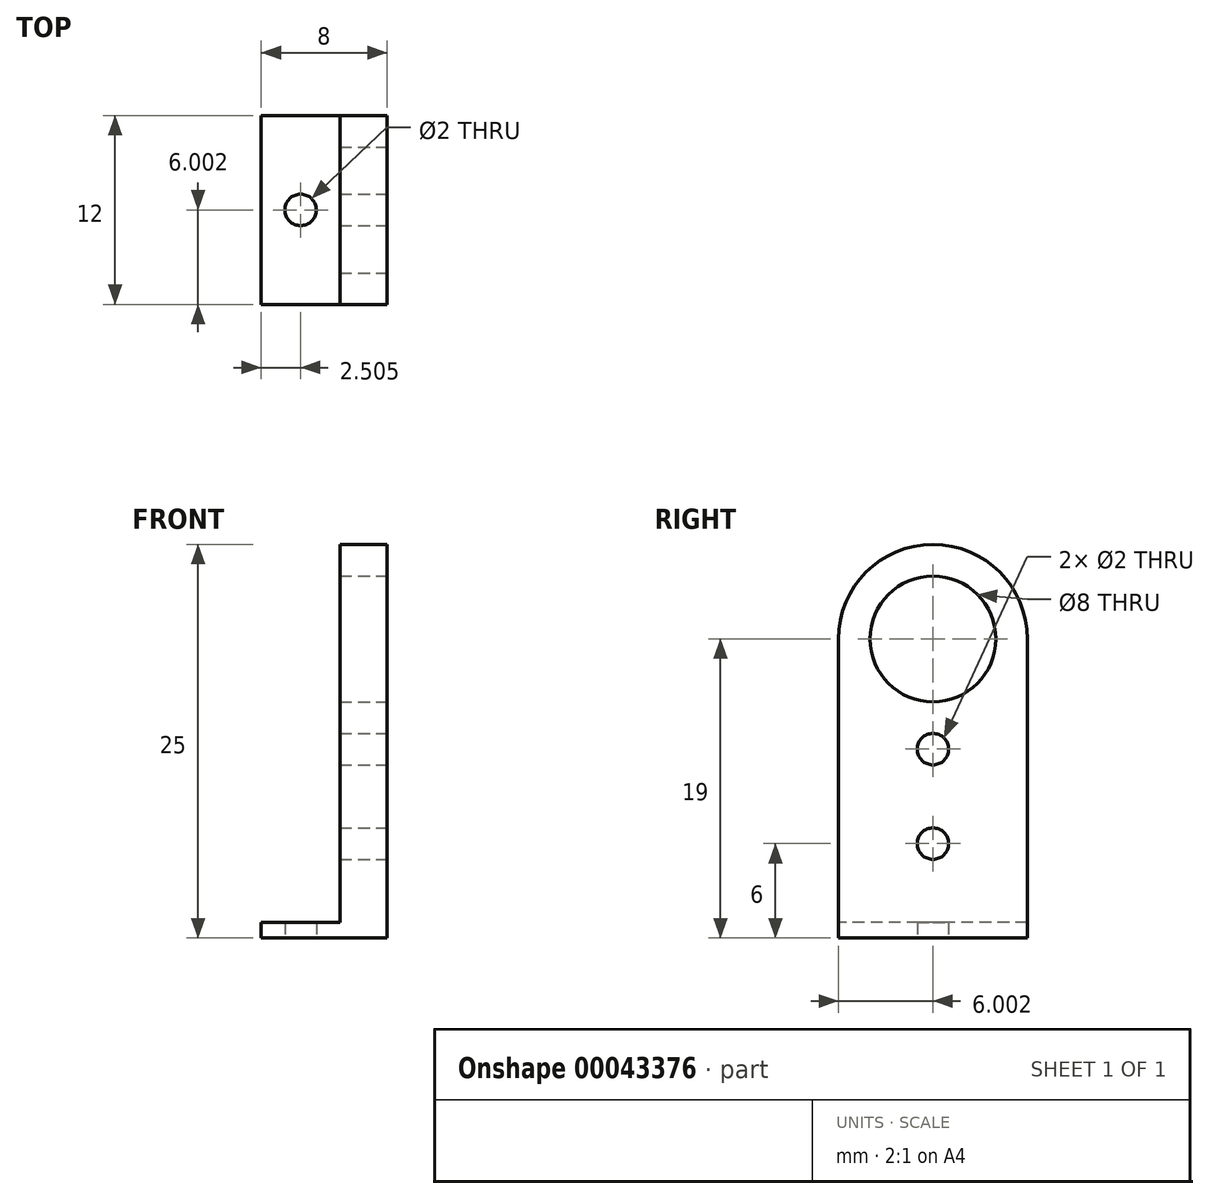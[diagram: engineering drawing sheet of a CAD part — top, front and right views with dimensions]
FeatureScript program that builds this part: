
annotation { "Feature Type Name" : "Feature", "Feature Type Description" : "" }
export const myFeature = defineFeature(function(context is Context, id is Id, definition is map)
    precondition{}
    {
        {
            var Q0;
            Q0=qCreatedBy(makeId("Top.planeOp"),FACE);
            var sketch = newSketch(context, id + "F0", { "sketchPlane" : qUnion([Q0])});
            skLineSegment(sketch, "E0.bottom", {"start": v(-17.45, 1.5) * mm, "end": v(-9.45, 1.5) * mm});
            skLineSegment(sketch, "E0.top", {"start": v(-17.45, -10.5) * mm, "end": v(-9.45, -10.5) * mm});
            skLineSegment(sketch, "E0.left", {"start": v(-17.45, 1.5) * mm, "end": v(-17.45, -10.5) * mm});
            skLineSegment(sketch, "E0.right", {"start": v(-9.45, 1.5) * mm, "end": v(-9.45, -10.5) * mm});
            skLineSegment(sketch, "E1", {"start": v(-17.45, -4.5) * mm, "end": v(-9.45, -4.5) * mm, "construction": true});
            skLineSegment(sketch, "E2", {"start": v(-13.45, 1.5) * mm, "end": v(-13.45, -10.5) * mm, "construction": true});
            skLineSegment(sketch, "E3", {"start": v(-12.45, 1.5) * mm, "end": v(-12.45, -10.5) * mm});
            skLineSegment(sketch, "E4", {"start": v(-12.45, 1.5) * mm, "end": v(-17.45, -10.5) * mm, "construction": true});
            skPoint(sketch, "E5", {"position": v(-14.95, -4.5) * mm});
            skCircle(sketch, "E6", {"center": v(-14.95, -4.5) * mm, "radius": 1 * mm});
            skSolve(sketch);
        }
        {
            var Q0;
            {var subQ2=sQuery(id+"F0.wireOp",EDGE,"E0.left");Q0=makeQuery(id+"F0.imprint","IMPRINT",FACE,{"disambiguationData":[TD([[makeQuery(id+"F0.imprint","IMPRINT",EDGE,{"derivedFrom":subQ2}),1.0]])]});}
            extrude(context, id + "F1", {"entities" : qUnion([Q0]), "depth" : 1 * mm});
        }
        {
            var Q0;
            {var subQ1=sQuery(id+"F0.wireOp",EDGE,"E0.right");Q0=makeQuery(id+"F0.imprint","IMPRINT",FACE,{"disambiguationData":[TD([[makeQuery(id+"F0.imprint","IMPRINT",EDGE,{"derivedFrom":subQ1}),-1.0]])]});}
            extrude(context, id + "F2", {"entities" : qUnion([Q0]), "operationType" : NewBodyOperationType.ADD, "depth" : 25 * mm});
        }
        {
            var Q0;
            Q0=makeQuery(id+"F2.opExtrude","SWEPT_FACE",FACE,{"disambiguationData":[OSD([sQuery(id+"F0.wireOp",EDGE,"E0.right")])]});
            var sketch = newSketch(context, id + "F3", { "sketchPlane" : qUnion([Q0])});
            skLineSegment(sketch, "E7.bottom", {"start": v(-10.5, 25) * mm, "end": v(1.5, 25) * mm, "construction": true});
            skLineSegment(sketch, "E7.top", {"start": v(-10.5, 0) * mm, "end": v(1.5, 0) * mm, "construction": true});
            skLineSegment(sketch, "E7.left", {"start": v(-10.5, 25) * mm, "end": v(-10.5, 0) * mm, "construction": true});
            skLineSegment(sketch, "E7.right", {"start": v(1.5, 25) * mm, "end": v(1.5, 0) * mm, "construction": true});
            skLineSegment(sketch, "E8", {"start": v(-4.5, 25) * mm, "end": v(-4.5, 0) * mm, "construction": true});
            skCircle(sketch, "E9", {"center": v(-4.5, 19) * mm, "radius": 4 * mm});
            skCircle(sketch, "E10", {"center": v(-4.5, 12) * mm, "radius": 1 * mm});
            skCircle(sketch, "E11", {"center": v(-4.5, 19) * mm, "radius": 3 * mm, "construction": true});
            skLineSegment(sketch, "E12", {"start": v(-10.5, 19) * mm, "end": v(1.5, 19) * mm, "construction": true});
            skCircle(sketch, "E13", {"center": v(-4.5, 6) * mm, "radius": 1 * mm});
            skSolve(sketch);
        }
        {
            var Q0;
            Q0=qSketchRegion(id+"F3",true);
            extrude(context, id + "F4", {"entities" : qUnion([Q0]), "operationType" : NewBodyOperationType.REMOVE, "oppositeDirection" : true, "depth" : 3 * mm});
        }
        {
            var Q0;
            Q0=makeQuery(id+"F2.opExtrude","CAP_EDGE",EDGE,{"disambiguationData":[OSD([sQuery(id+"F0.wireOp",EDGE,"E0.bottom")])],"isStart":false});
            var Q1;
            Q1=makeQuery(id+"F2.opExtrude","CAP_EDGE",EDGE,{"disambiguationData":[OSD([sQuery(id+"F0.wireOp",EDGE,"E0.top")])],"isStart":false});
            fillet(context, id + "F5", {"entities" : qUnion([Q0, Q1]), "radius" : 6 * mm, "tangentPropagation" : true, "allowEdgeOverflow" : false});
        }
    });
